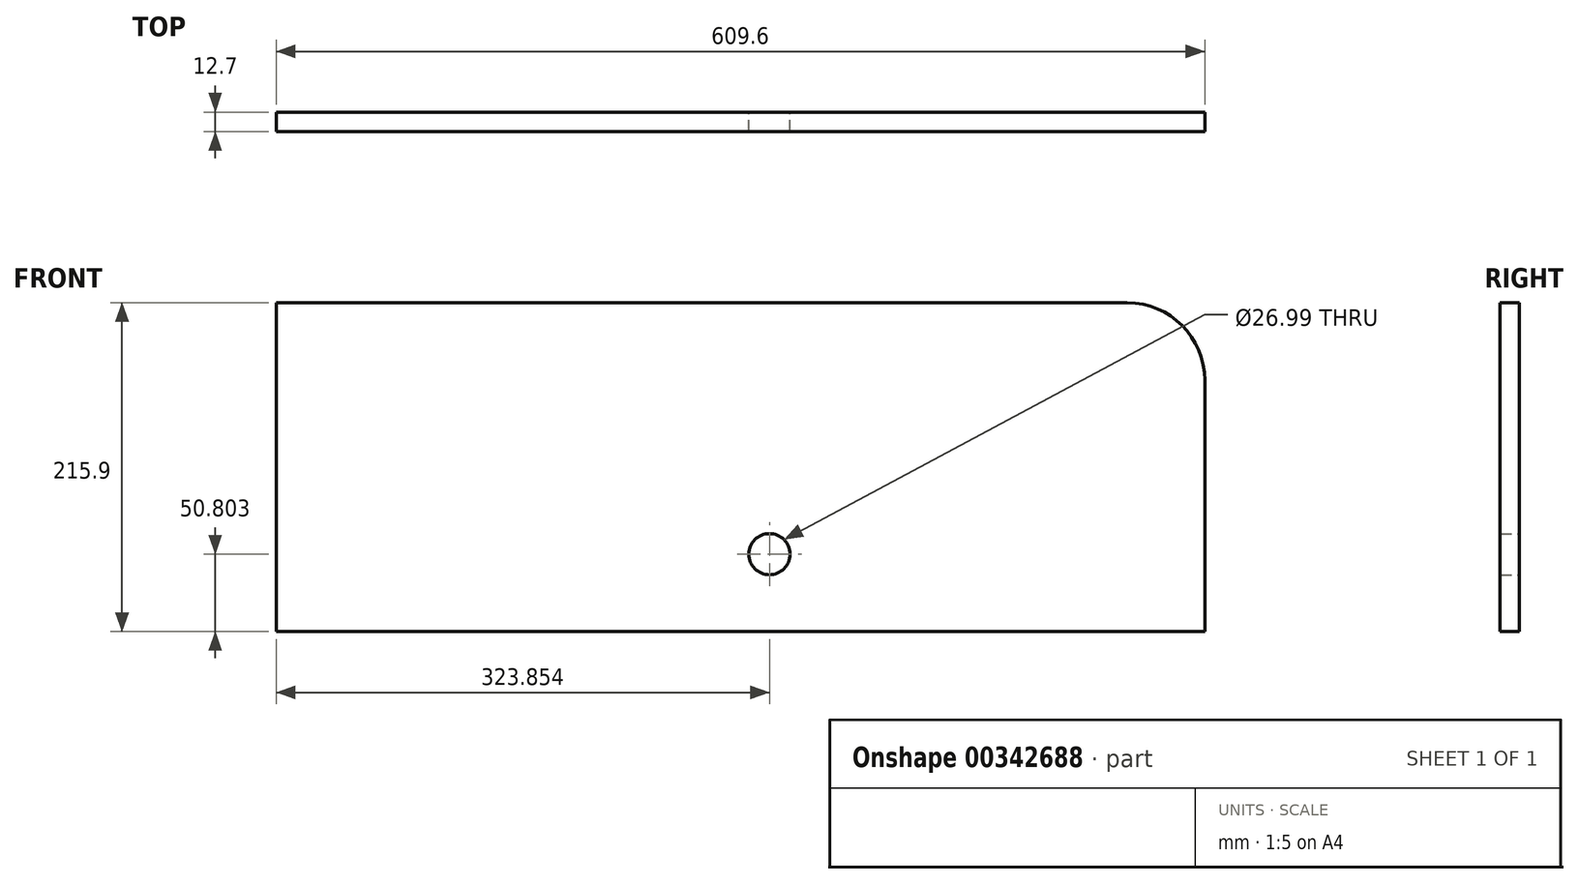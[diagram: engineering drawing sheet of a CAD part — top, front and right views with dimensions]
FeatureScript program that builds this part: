
annotation { "Feature Type Name" : "Feature", "Feature Type Description" : "" }
export const myFeature = defineFeature(function(context is Context, id is Id, definition is map)
    precondition{}
    {
        {
            var Q0;
            Q0=qCreatedBy(makeId("Front.planeOp"),FACE);
            var sketch = newSketch(context, id + "F0", { "sketchPlane" : qUnion([Q0])});
            skLineSegment(sketch, "E0.bottom", {"start": v(-312.56, 52.37) * mm, "end": v(246.24, 52.37) * mm});
            skLineSegment(sketch, "E0.top", {"start": v(-312.56, -163.53) * mm, "end": v(297.04, -163.53) * mm});
            skLineSegment(sketch, "E0.left", {"start": v(-312.56, 52.37) * mm, "end": v(-312.56, -163.53) * mm});
            skLineSegment(sketch, "E0.right", {"start": v(297.04, 1.57) * mm, "end": v(297.04, -163.53) * mm});
            skPoint(sketch, "E1.visualSharp", {"position": v(297.04, 52.37) * mm});
            skArc(sketch, "E1.filletArc", {"start": v(297.04, 1.57) * mm, "mid": v(282.16, 37.5) * mm, "end": v(246.24, 52.37) * mm});
            skCircle(sketch, "E2", {"center": v(11.3, -112.73) * mm, "radius": 13.5 * mm});
            skSolve(sketch);
        }
        {
            var Q0;
            Q0=makeQuery(id+"F0.imprint","IMPRINT",FACE,{"disambiguationData":[TD([[makeQuery(id+"F0.imprint","IMPRINT",EDGE,{"derivedFrom":sQuery(id+"F0.wireOp",EDGE,"E0.bottom")}),-1.0]])]});
            extrude(context, id + "F1", {"entities" : qUnion([Q0]), "depth" : 12.7 * mm});
        }
    });
